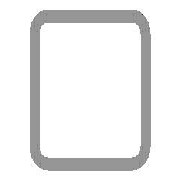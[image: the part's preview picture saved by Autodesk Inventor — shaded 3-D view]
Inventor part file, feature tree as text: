
AUTODESK INVENTOR PART (.ipt)
format: ipt  version: 2025 (Build 290162010, 162A)  size: 135,168 bytes
history: native  units: mm (DEFAULTED — no unit token found)
features: other x4, sketch x1, plane x1
ambient origin geometry x8: Origin, YZ Plane, XZ Plane, XY Plane, X Axis, Y Axis, Z Axis, Center Point
bodies: Solid1 (feature_tree), Body (feature_tree)
feature tree (6):
  parser-record x1  (decoder bookkeeping rows leaked as tree rows — omitted from the tree; the rows remain in map.json)
  other  "Driven Length"
  other  "Start Plane"
  other  "End Plane"
  sketch  "Sketch3"  dims[d3=3200.0mm d4=0.0mm d7=6.0mm d9=80.0mm d11=80.0mm d12=3.0mm d13=-0.0mm d14=3200.0mm d15=40.0mm d16=40.0mm d17=90.0deg d18=3200.0mm]
  plane  "Work Plane3"
